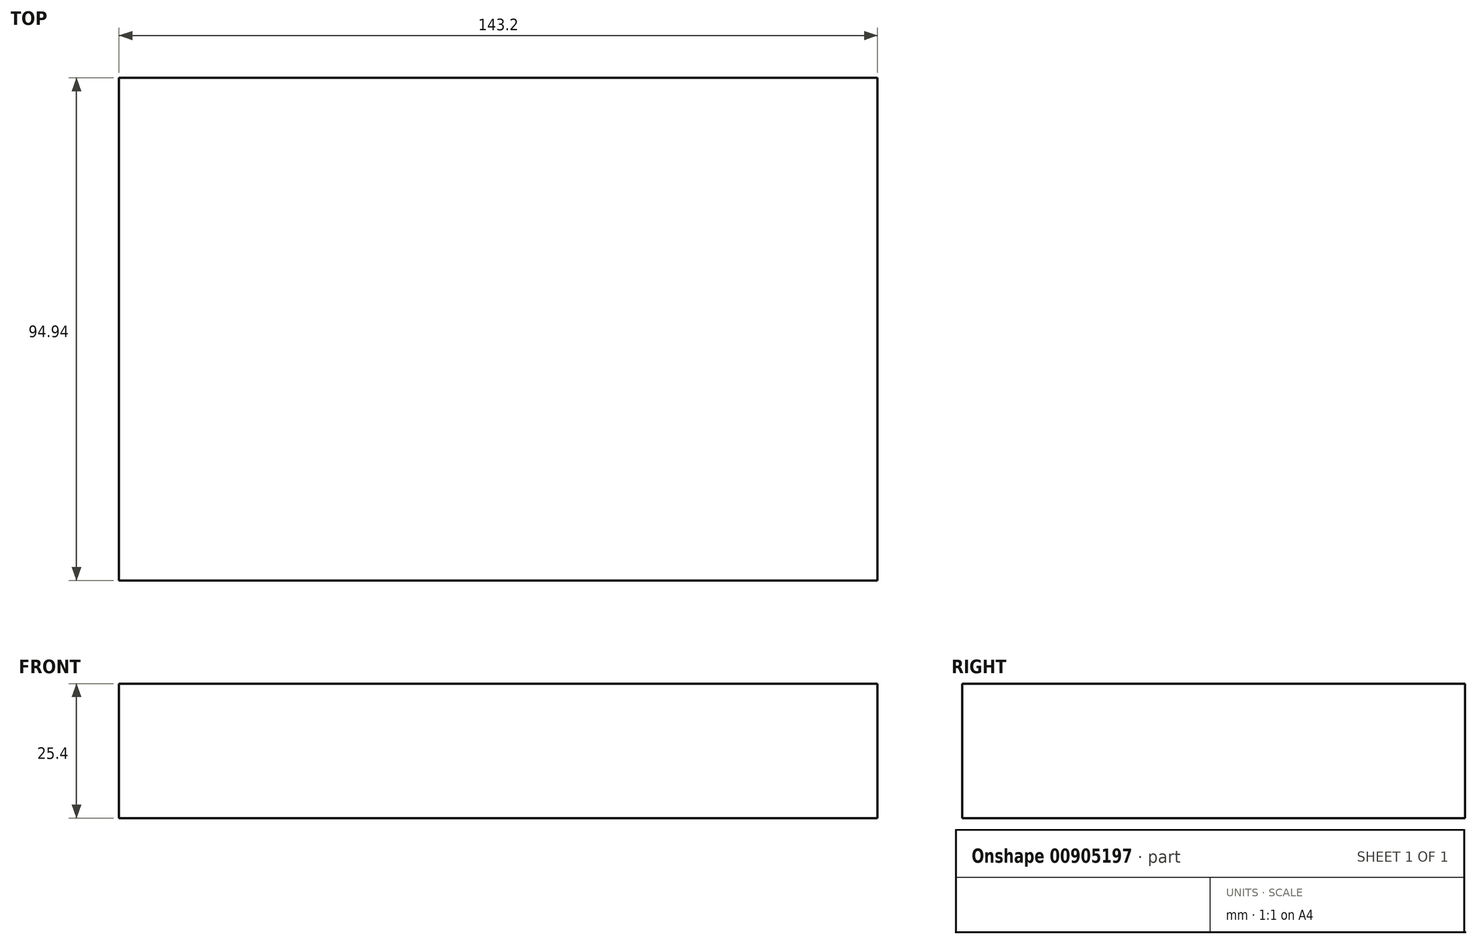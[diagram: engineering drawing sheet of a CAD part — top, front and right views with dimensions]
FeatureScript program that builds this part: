
annotation { "Feature Type Name" : "Feature", "Feature Type Description" : "" }
export const myFeature = defineFeature(function(context is Context, id is Id, definition is map)
    precondition{}
    {
        {
            var Q0;
            Q0=qCreatedBy(makeId("Top.planeOp"),FACE);
            var sketch = newSketch(context, id + "F0", { "sketchPlane" : qUnion([Q0])});
            skLineSegment(sketch, "E0.bottom", {"start": v(71.6, 47.47) * mm, "end": v(-71.6, 47.47) * mm});
            skLineSegment(sketch, "E0.top", {"start": v(71.6, -47.47) * mm, "end": v(-71.6, -47.47) * mm});
            skLineSegment(sketch, "E0.left", {"start": v(71.6, 47.47) * mm, "end": v(71.6, -47.47) * mm});
            skLineSegment(sketch, "E0.right", {"start": v(-71.6, 47.47) * mm, "end": v(-71.6, -47.47) * mm});
            skPoint(sketch, "E0.middle", {"position": v(0, 0) * mm});
            skSolve(sketch);
        }
        {
            var Q0;
            Q0=makeQuery(id+"F0.imprint","IMPRINT",FACE,{"disambiguationData":[TD([[makeQuery(id+"F0.imprint","IMPRINT",EDGE,{"derivedFrom":sQuery(id+"F0.wireOp",EDGE,"E0.bottom")}),1.0]])]});
            extrude(context, id + "F1", {"entities" : qUnion([Q0]), "depth" : 25.4 * mm, "offsetDistance" : 25.4 * mm});
        }
    });
